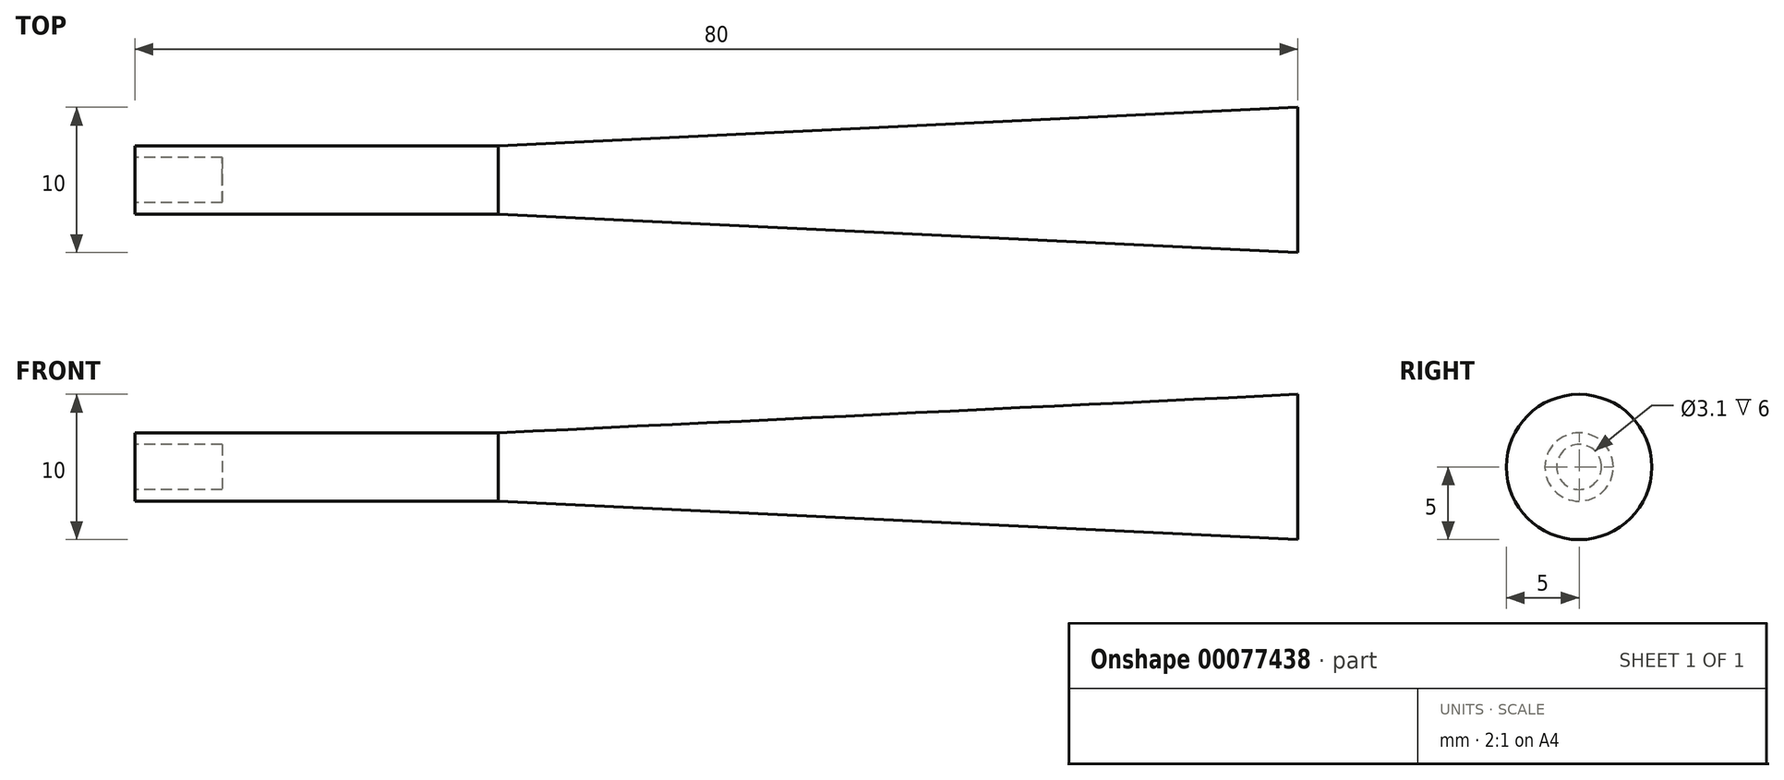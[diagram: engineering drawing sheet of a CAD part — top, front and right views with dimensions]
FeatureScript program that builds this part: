
annotation { "Feature Type Name" : "Feature", "Feature Type Description" : "" }
export const myFeature = defineFeature(function(context is Context, id is Id, definition is map)
    precondition{}
    {
        {
            var Q0;
            Q0=qCreatedBy(makeId("Front.planeOp"),FACE);
            var sketch = newSketch(context, id + "F0", { "sketchPlane" : qUnion([Q0])});
            skLineSegment(sketch, "E0", {"start": v(0, 0) * mm, "end": v(12.7, 0) * mm});
            skLineSegment(sketch, "E1", {"start": v(0, 1.55) * mm, "end": v(6, 1.55) * mm});
            skLineSegment(sketch, "E2", {"start": v(6, 1.55) * mm, "end": v(6, 0) * mm});
            skLineSegment(sketch, "E3", {"start": v(6, 0) * mm, "end": v(80, 0) * mm});
            skLineSegment(sketch, "E4", {"start": v(80, 0) * mm, "end": v(80, 5) * mm});
            skLineSegment(sketch, "E5", {"start": v(80, 5) * mm, "end": v(25, 2.35) * mm});
            skLineSegment(sketch, "E6", {"start": v(25, 2.35) * mm, "end": v(0, 2.35) * mm});
            skLineSegment(sketch, "E7", {"start": v(0, 2.35) * mm, "end": v(0, 1.55) * mm});
            skLineSegment(sketch, "E8.MirrorCS", {"start": v(6, -1.55) * mm, "end": v(6, 0) * mm});
            skLineSegment(sketch, "E9.MirrorCS", {"start": v(0, -1.55) * mm, "end": v(6, -1.55) * mm});
            skLineSegment(sketch, "E10.MirrorCS", {"start": v(0, -2.35) * mm, "end": v(0, -1.55) * mm});
            skLineSegment(sketch, "E11.MirrorCS", {"start": v(25, -2.35) * mm, "end": v(0, -2.35) * mm});
            skLineSegment(sketch, "E12.MirrorCS", {"start": v(80, -5) * mm, "end": v(25, -2.35) * mm});
            skLineSegment(sketch, "E13.MirrorCS", {"start": v(80, 0) * mm, "end": v(80, -5) * mm});
            skSolve(sketch);
        }
        {
            var Q0;
            Q0=makeQuery(id+"F0.imprint","IMPRINT",FACE,{"disambiguationData":[TD([[makeQuery(id+"F0.imprint","IMPRINT",EDGE,{"derivedFrom":sQuery(id+"F0.wireOp",EDGE,"E1")}),1.0]])]});
            var Q1;
            Q1=sQuery(id+"F0.wireOp",EDGE,"E3");
            revolve(context, id + "F1", {"entities" : qUnion([Q0]), "axis" : qUnion([Q1]), "revolveType" : RevolveType.FULL});
        }
    });
